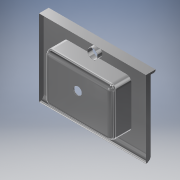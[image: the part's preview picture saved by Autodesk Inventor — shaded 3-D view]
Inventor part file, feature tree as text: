
AUTODESK INVENTOR PART (.ipt)
format: ipt  version: 2016 (Build 200138000, 138)  size: 367,616 bytes
history: native  units: mm
features: sketch x19, extrude x7, revolve x4, sweep x4, other x1, fillet x1, shell x1
ambient origin geometry x8: Origin, YZ Plane, XZ Plane, XY Plane, X Axis, Y Axis, Z Axis, Center Point
bodies: Body1 (feature_tree)
feature tree (37):
  other  "Sólido1"
  sketch  "Boceto1"  dims[d2=700.0mm d3=500.0mm]
  extrude  "Extrusión1"  Depth=500.0mm
  revolve  "Revolución1"  [1 undecoded]
  revolve  "Revolución2"  Angle=90.0deg
  revolve  "Revolución3"  Angle=90.0deg
  revolve  "Revolución4"  [1 undecoded]
  extrude  "Extrusión2"  TaperAngle=0.0deg  [1 undecoded]
  sweep  "Barrido1"
  sweep  "Barrido2"
  sweep  "Barrido3"
  sweep  "Barrido4"
  extrude  "Extrusión3"  Depth=50.0mm
  extrude  "Extrusión4"  Depth=50.0mm
  extrude  "Extrusión6"  Depth=20.0mm
  fillet  "Fillet1"  Radius=20.0mm
  extrude  "Extrusion11"  Depth=100.0mm
  extrude  "Extrusion12"  Depth=10.0mm TaperAngle=0.0deg
  shell  "Shell1"  Thickness=1.0mm
  sketch  "Boceto3"  dims[d13=90.0deg d14=90.0deg]
  sketch  "Boceto4"  dims[d18=0.0mm d19=0.0mm]
  sketch  "Boceto5"  dims[d22=80.0mm d23=10.0mm d24=0.0mm]
  sketch  "Boceto6"  dims[d25=100.0mm d26=3.0mm d27=0.0mm]
  sketch  "Boceto7"  dims[d29=0.0mm d30=0.0mm d31=0.0mm d32=0.0mm d41=700.0mm]
  sketch  "Boceto8"  dims[d42=500.0mm d43=50.0mm]
  sketch  "Boceto 3D1"  dims[d4=2.0mm d5=50.0mm]
  sketch  "Boceto9"  dims[d44=50.0mm d45=0.0mm d67=50.0mm]
  sketch  "Boceto 3D2"  dims[d10=150.0mm d11=0.0mm d12=90.0deg]
  sketch  "Boceto10"  dims[d71=101.6mm d72=255.0mm d73=20.0mm d74=0.0mm]
  sketch  "Boceto 3D3"  dims[d15=90.0deg d16=400.0mm d17=0.0mm]
  sketch  "Boceto11"  dims[d75=20.0mm d76=100.0mm]
  sketch  "Boceto 3D4"  dims[d20=0.0mm d21=0.0mm]
  sketch  "Boceto12"  dims[d77=20.0mm d78=10.0mm d79=0.0mm d80=1.0mm]
  sketch  "Boceto13"  dims[d81=200.0mm]
  sketch  "Boceto15"  dims[d82=350.0mm]
  sketch  "Sketch21"
  sketch  "Sketch22"
note: 3 required parameter values undecoded (feature->parameter linkage not recoverable at this tier; creation-order binding heuristic only, values carry confidence <= 0.55)